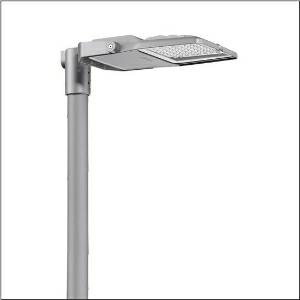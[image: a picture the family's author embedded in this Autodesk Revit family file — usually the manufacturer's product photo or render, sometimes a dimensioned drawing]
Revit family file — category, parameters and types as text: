
# Revit family: floodlight_fl_21_mini___pl43_5xa7776c4a3a_ef43
name_source: partatom
category: Lighting Fixtures
units: mm (PartAtom-declared; Revit-internal decimal feet)

## family parameters
Cut with Voids When Loaded = No
Host = Face
Light Source = No
Part Type = Normal
Room Calculation Point = No
Round Connector Dimension = Use Diameter
Shared = No

## types (1)
- --- (1 x LED, 13020 lm, 89 W, 4000K)
    Apparent Load = 89 VA
    CIE Flux Codes = 27 78 99 100 100
    Color Rendering = 70
    Color Temperature = 4000K
    Default Elevation = 1800 mm
    Description = Floodlight FL 21 mini, floodlight, primary light control with lens, of PMMA, primary optical cover: protective disc, of toughened safety glass, transparent, light distribution: PL43, light emission: direct distribution, installation type: surface-mounted, LED, High Power LED, rated luminous flux: 13.020lm, luminous efficacy: 146lm/W, light colour: 740, colour temperature: 4000K, control gear: Smart Interface (Zhaga), control: pre-setting: logarithmic dimming characteristic, flexible luminous flux parameterisation, time-dependent luminous flux control, constant luminous flux control, overheat protection, with terminal, 6-pole, mains connection: 220..240V, AC, 50/60Hz, start of lifetime: 89W, end of service life: 94W, reduction: 43W, luminaire housing, of diecast aluminium, powder-coated, SITECO metallic grey (DB 702S), corrosivity category C5 mid according to DIN EN ISO 12944, suitable for swimming pools, chlorine-resistant, sealing non-destructively replaceable, please order mast flange separately, mast bracket, of steel, galvanised, powder-coated, SITECO metallic grey (DB 702S), Smart Interface below and above, protection rating (complete): IP66, insulation class (complete): insulation class II (safety insulation), certification: CE, ENEC, VDE, protection symbol: D, impact resistance: IK08, permissible operating ambient temperature: -40..+40°C, permissible operating ambient temperature for outdoor applications: -40..+50°C, standard: DIN EN 12944, LABS conformity tested according to VDMA 24364:2018-05, packaging unit: 1 piece

Light Distribution: PL43
    Height = 70 mm
    Lamp = 1 x LED
    Lamp Light Flux = 13020 lm
    Lamp Power = 89 W
    Lamp count = 1
    Length = 485 mm
    Luminous efficacy = 146 lm/W
    Manufacturer = Siteco
    ModVariant = No
    Model = 5XA7776C4A3A
    Number of Poles = 1
    OnlyDefault = Yes
    Power Factor = 1
    Product Name = Floodlight FL 21 mini | PL43
    Product group = floodlight | pylon annexe
    ProductGroupID = 6201
    Protection Class = Protection class II
    Protection Degree = IP 66
    RLX_Detail_Level = 1
    RLX_Emergency_Light_Flux = 0 lm
    RLX_Emergency_Type = 0
    RLX_Emergency_Type_DB = No
    RlxData = <blob elided: 101005 chars, md5=e1047916>
    Socket = socket
    Standby Power = 0 W
    System Light Flux = 13020 lm
    System Power = 89 W
    Type Comments = factory setting: luminous flux: 100 % | dim-lin: 254 | 456 mA
    Type Image = l_1007125.jpg
    URL = http://relux.com
    VarID = @adj_099163
    Voltage = 0 V
    Weight = 0.00 kg
    Width = 337 mm

## geometry (parser evidence)
native form markers: Blend x4, Sweep x12
no freeform markers — native parametric forms only
